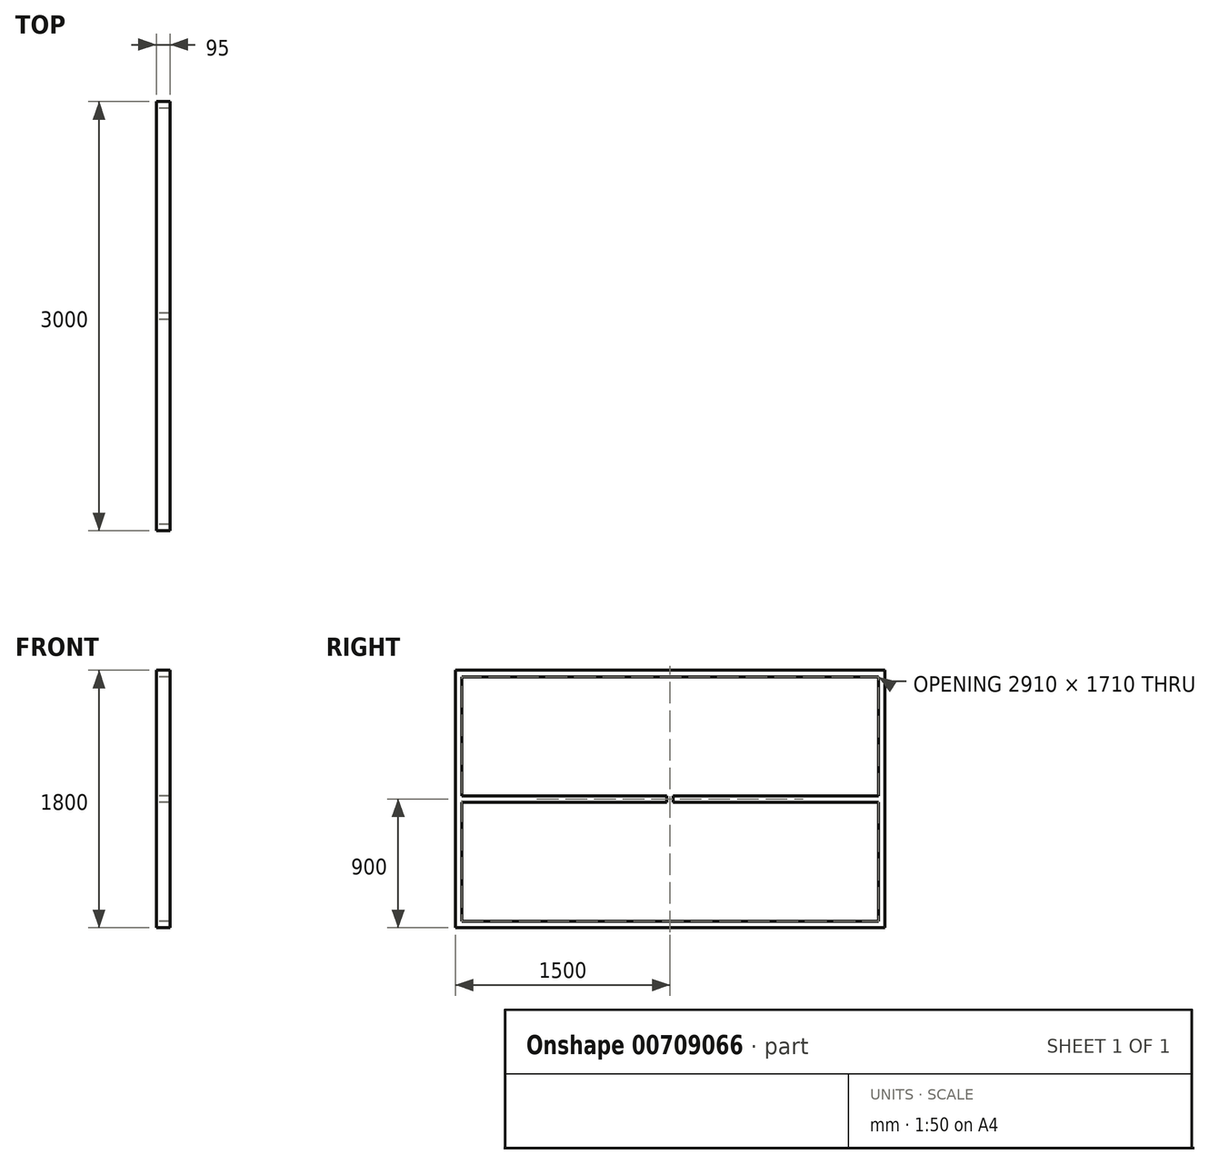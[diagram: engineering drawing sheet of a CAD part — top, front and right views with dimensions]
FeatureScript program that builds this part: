
annotation { "Feature Type Name" : "Feature", "Feature Type Description" : "" }
export const myFeature = defineFeature(function(context is Context, id is Id, definition is map)
    precondition{}
    {
        {
            var Q0;
            Q0=qCreatedBy(makeId("Right.planeOp"),FACE);
            var sketch = newSketch(context, id + "F0", { "sketchPlane" : qUnion([Q0])});
            skLineSegment(sketch, "E0.bottom", {"start": v(-1500, 900) * mm, "end": v(1500, 900) * mm});
            skLineSegment(sketch, "E0.top", {"start": v(-1500, -900) * mm, "end": v(1500, -900) * mm});
            skLineSegment(sketch, "E0.left", {"start": v(-1500, 900) * mm, "end": v(-1500, -900) * mm});
            skLineSegment(sketch, "E0.right", {"start": v(1500, 900) * mm, "end": v(1500, -900) * mm});
            skPoint(sketch, "E0.middle", {"position": v(0, 0) * mm});
            skLineSegment(sketch, "E1", {"start": v(-1500, 855) * mm, "end": v(1500, 855) * mm});
            skLineSegment(sketch, "E2", {"start": v(-1500, -855) * mm, "end": v(1500, -855) * mm});
            skLineSegment(sketch, "E3", {"start": v(1455, 855) * mm, "end": v(1455, -855) * mm});
            skLineSegment(sketch, "E4", {"start": v(-1455, 855) * mm, "end": v(-1455, -855) * mm});
            skLineSegment(sketch, "E5.bottom", {"start": v(-22.5, 855) * mm, "end": v(22.5, 855) * mm});
            skLineSegment(sketch, "E5.top", {"start": v(-22.5, -855) * mm, "end": v(22.5, -855) * mm});
            skLineSegment(sketch, "E5.left", {"start": v(-22.5, 855) * mm, "end": v(-22.5, -855) * mm});
            skLineSegment(sketch, "E5.right", {"start": v(22.5, 855) * mm, "end": v(22.5, -855) * mm});
            skLineSegment(sketch, "E6", {"start": v(-1455, 22.5) * mm, "end": v(-22.5, 22.5) * mm});
            skLineSegment(sketch, "E7", {"start": v(-1455, -22.5) * mm, "end": v(-22.5, -22.5) * mm});
            skLineSegment(sketch, "E8.bottom", {"start": v(22.5, 22.5) * mm, "end": v(1455, 22.5) * mm});
            skLineSegment(sketch, "E8.top", {"start": v(22.5, -22.5) * mm, "end": v(1455, -22.5) * mm});
            skLineSegment(sketch, "E8.left", {"start": v(22.5, 22.5) * mm, "end": v(22.5, -22.5) * mm});
            skLineSegment(sketch, "E8.right", {"start": v(1455, 22.5) * mm, "end": v(1455, -22.5) * mm});
            skSolve(sketch);
        }
        {
            var Q0;
            Q0 = qSketchRegion(id + "F0", true);
            var Q1;
            {var subQ0=sQuery(id+"F0.wireOp",EDGE,"E6");Q1=makeQuery(id+"F0.imprint","IMPRINT",FACE,{"disambiguationData":[TD([[makeQuery(id+"F0.imprint","IMPRINT",EDGE,{"derivedFrom":subQ0}),-1.0]])]});}
            var Q2;
            Q2=makeQuery(id+"F0.imprint","IMPRINT",FACE,{"disambiguationData":[TD([[makeQuery(id+"F0.imprint","IMPRINT",EDGE,{"derivedFrom":sQuery(id+"F0.wireOp",EDGE,"E8.bottom")}),-1.0]])]});
            var Q3;
            {var subQ3=sQuery(id+"F0.wireOp",EDGE,"E5.bottom");Q3=makeQuery(id+"F0.imprint","IMPRINT",FACE,{"disambiguationData":[TD([[makeQuery(id+"F0.imprint","IMPRINT",EDGE,{"derivedFrom":subQ3}),-1.0]])]});}
            extrude(context, id + "F1", {"entities" : qUnion([Q0, Q1, Q2, Q3]), "depth" : 95 * mm, "offsetDistance" : 25 * mm});
        }
    });
